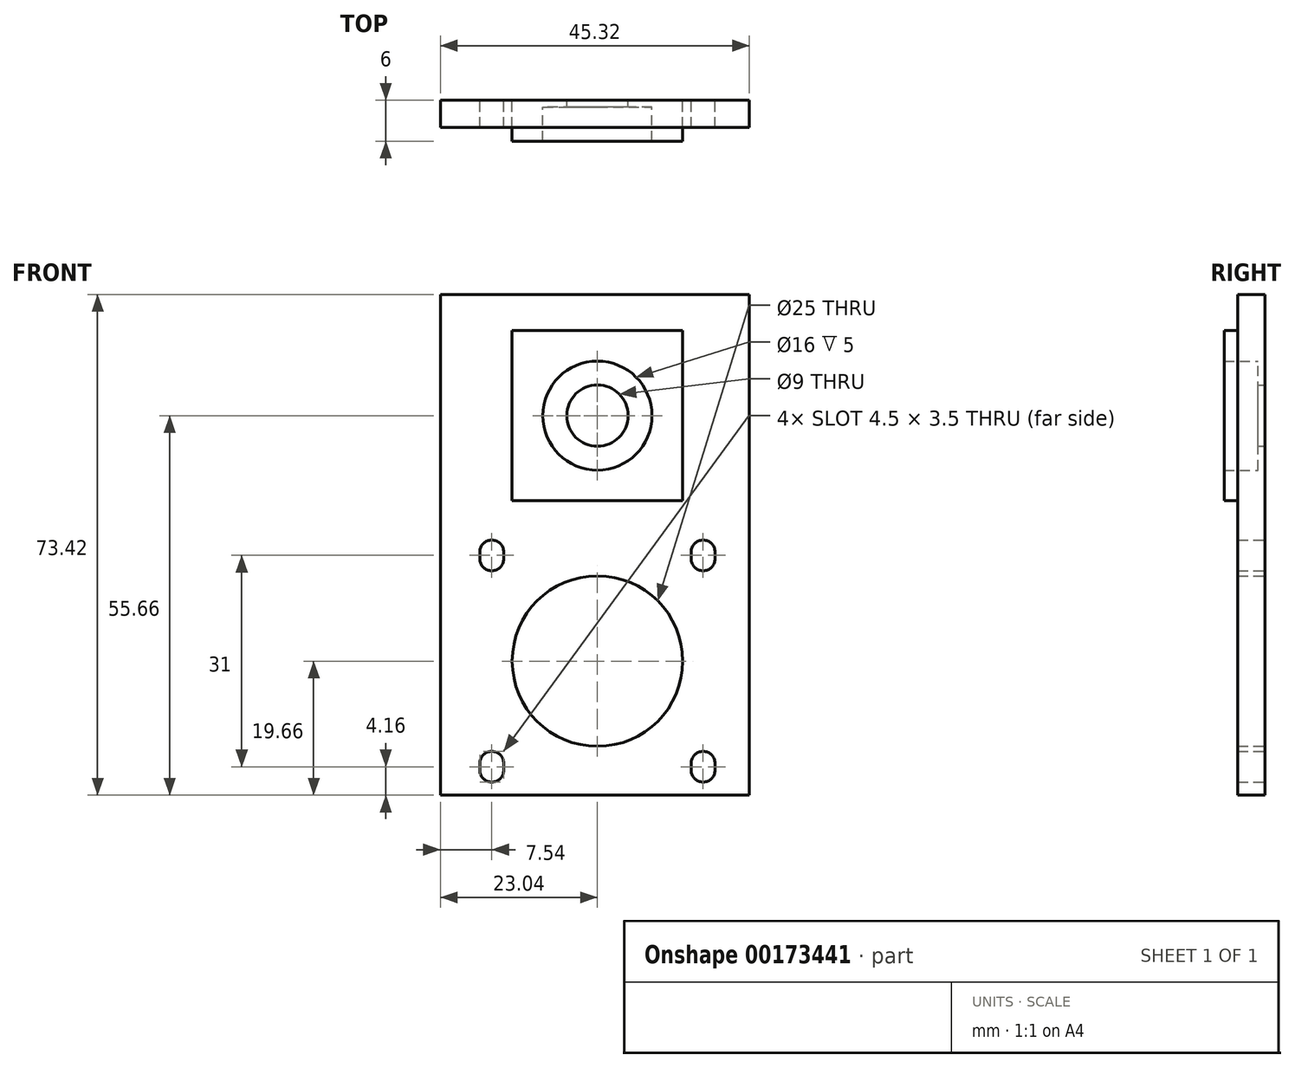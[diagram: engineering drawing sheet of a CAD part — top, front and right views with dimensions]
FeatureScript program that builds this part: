
annotation { "Feature Type Name" : "Feature", "Feature Type Description" : "" }
export const myFeature = defineFeature(function(context is Context, id is Id, definition is map)
    precondition{}
    {
        {
            var Q0;
            Q0=qCreatedBy(makeId("Front.planeOp"),FACE);
            var sketch = newSketch(context, id + "F0", { "sketchPlane" : qUnion([Q0])});
            skCircle(sketch, "E0", {"center": v(0, 0) * mm, "radius": 4.5 * mm});
            skCircle(sketch, "E1", {"center": v(0, -36) * mm, "radius": 12.5 * mm});
            skCircle(sketch, "E2", {"center": v(0, 0) * mm, "radius": 8 * mm});
            skLineSegment(sketch, "E3", {"start": v(-31.18, -36) * mm, "end": v(32.54, -36) * mm, "construction": true});
            skLineSegment(sketch, "E4.bottom", {"start": v(22.28, -55.66) * mm, "end": v(-23.04, -55.66) * mm});
            skLineSegment(sketch, "E4.top", {"start": v(22.28, 17.76) * mm, "end": v(-23.04, 17.76) * mm});
            skLineSegment(sketch, "E4.left", {"start": v(22.28, -55.66) * mm, "end": v(22.28, 17.76) * mm});
            skLineSegment(sketch, "E4.right", {"start": v(-23.04, -55.66) * mm, "end": v(-23.04, 17.76) * mm});
            skLineSegment(sketch, "E5", {"start": v(-15.5, -20) * mm, "end": v(-15.5, -21) * mm, "construction": true});
            skPoint(sketch, "E6", {"position": v(-15.5, -20.5) * mm});
            skArc(sketch, "E7", {"start": v(-13.75, -20) * mm, "mid": v(-15.5, -18.25) * mm, "end": v(-17.25, -20) * mm});
            skArc(sketch, "E8", {"start": v(-17.25, -21) * mm, "mid": v(-15.5, -22.75) * mm, "end": v(-13.75, -21) * mm});
            skLineSegment(sketch, "E9", {"start": v(-17.25, -20) * mm, "end": v(-17.25, -21) * mm});
            skLineSegment(sketch, "E10", {"start": v(-13.75, -20) * mm, "end": v(-13.75, -21) * mm});
            skArc(sketch, "E11.MirrorCS", {"start": v(-13.75, -21) * mm, "mid": v(-15.5, -22.75) * mm, "end": v(-17.25, -21) * mm});
            skArc(sketch, "E12.MirrorCS", {"start": v(-17.25, -20) * mm, "mid": v(-15.5, -18.25) * mm, "end": v(-13.75, -20) * mm});
            skLineSegment(sketch, "E13.MirrorCS", {"start": v(13.75, -20) * mm, "end": v(13.75, -21) * mm});
            skLineSegment(sketch, "E14.MirrorCS", {"start": v(17.25, -20) * mm, "end": v(17.25, -21) * mm});
            skLineSegment(sketch, "E15.MirrorCS", {"start": v(15.5, -20) * mm, "end": v(15.5, -21) * mm, "construction": true});
            skPoint(sketch, "E16.MirrorP", {"position": v(15.5, -20.5) * mm});
            skArc(sketch, "E17.MirrorCS", {"start": v(13.75, -21) * mm, "mid": v(15.5, -22.75) * mm, "end": v(17.25, -21) * mm});
            skArc(sketch, "E18.MirrorCS", {"start": v(13.75, -20) * mm, "mid": v(15.5, -18.25) * mm, "end": v(17.25, -20) * mm});
            skArc(sketch, "E19.MirrorCS", {"start": v(17.25, -20) * mm, "mid": v(15.5, -18.25) * mm, "end": v(13.75, -20) * mm});
            skArc(sketch, "E20.MirrorCS", {"start": v(17.25, -21) * mm, "mid": v(15.5, -22.75) * mm, "end": v(13.75, -21) * mm});
            skLineSegment(sketch, "E21.MirrorCS", {"start": v(-17.25, -52) * mm, "end": v(-17.25, -51) * mm});
            skLineSegment(sketch, "E22.MirrorCS", {"start": v(-13.75, -52) * mm, "end": v(-13.75, -51) * mm});
            skLineSegment(sketch, "E23.MirrorCS", {"start": v(-15.5, -52) * mm, "end": v(-15.5, -51) * mm, "construction": true});
            skArc(sketch, "E24.MirrorCS", {"start": v(-13.75, -51) * mm, "mid": v(-15.5, -49.25) * mm, "end": v(-17.25, -51) * mm});
            skPoint(sketch, "E25.MirrorP", {"position": v(-15.5, -51.5) * mm});
            skArc(sketch, "E26.MirrorCS", {"start": v(-13.75, -52) * mm, "mid": v(-15.5, -53.75) * mm, "end": v(-17.25, -52) * mm});
            skArc(sketch, "E27.MirrorCS", {"start": v(-17.25, -51) * mm, "mid": v(-15.5, -49.25) * mm, "end": v(-13.75, -51) * mm});
            skArc(sketch, "E28.MirrorCS", {"start": v(-17.25, -52) * mm, "mid": v(-15.5, -53.75) * mm, "end": v(-13.75, -52) * mm});
            skLineSegment(sketch, "E29.MirrorCS", {"start": v(17.25, -52) * mm, "end": v(17.25, -51) * mm});
            skLineSegment(sketch, "E30.MirrorCS", {"start": v(13.75, -52) * mm, "end": v(13.75, -51) * mm});
            skLineSegment(sketch, "E31.MirrorCS", {"start": v(15.5, -52) * mm, "end": v(15.5, -51) * mm, "construction": true});
            skArc(sketch, "E32.MirrorCS", {"start": v(13.75, -51) * mm, "mid": v(15.5, -49.25) * mm, "end": v(17.25, -51) * mm});
            skArc(sketch, "E33.MirrorCS", {"start": v(13.75, -52) * mm, "mid": v(15.5, -53.75) * mm, "end": v(17.25, -52) * mm});
            skPoint(sketch, "E34.MirrorP", {"position": v(15.5, -51.5) * mm});
            skArc(sketch, "E35.MirrorCS", {"start": v(17.25, -51) * mm, "mid": v(15.5, -49.25) * mm, "end": v(13.75, -51) * mm});
            skArc(sketch, "E36.MirrorCS", {"start": v(17.25, -52) * mm, "mid": v(15.5, -53.75) * mm, "end": v(13.75, -52) * mm});
            skLineSegment(sketch, "E37.bottom", {"start": v(12.5, 12.5) * mm, "end": v(-12.5, 12.5) * mm});
            skLineSegment(sketch, "E37.top", {"start": v(12.5, -12.5) * mm, "end": v(-12.5, -12.5) * mm});
            skLineSegment(sketch, "E37.left", {"start": v(12.5, 12.5) * mm, "end": v(12.5, -12.5) * mm});
            skLineSegment(sketch, "E37.right", {"start": v(-12.5, 12.5) * mm, "end": v(-12.5, -12.5) * mm});
            skSolve(sketch);
        }
        {
            var Q0;
            Q0=makeQuery(id+"F0.imprint","IMPRINT",FACE,{"disambiguationData":[TD([[makeQuery(id+"F0.imprint","IMPRINT",EDGE,{"derivedFrom":sQuery(id+"F0.wireOp",EDGE,"E1")}),-1.0]])]});
            extrude(context, id + "F1", {"entities" : qUnion([Q0]), "depth" : 4 * mm});
        }
        {
            var Q0;
            Q0=makeQuery(id+"F0.imprint","IMPRINT",FACE,{"disambiguationData":[TD([[makeQuery(id+"F0.imprint","IMPRINT",EDGE,{"derivedFrom":sQuery(id+"F0.wireOp",EDGE,"E2")}),-1.0]])]});
            extrude(context, id + "F2", {"entities" : qUnion([Q0]), "operationType" : NewBodyOperationType.ADD, "depth" : 6 * mm});
        }
        {
            var Q0;
            Q0=makeQuery(id+"F0.imprint","IMPRINT",FACE,{"disambiguationData":[TD([[makeQuery(id+"F0.imprint","IMPRINT",EDGE,{"derivedFrom":sQuery(id+"F0.wireOp",EDGE,"E0")}),-1.0]])]});
            extrude(context, id + "F3", {"entities" : qUnion([Q0]), "operationType" : NewBodyOperationType.ADD, "depth" : 1 * mm});
        }
    });
